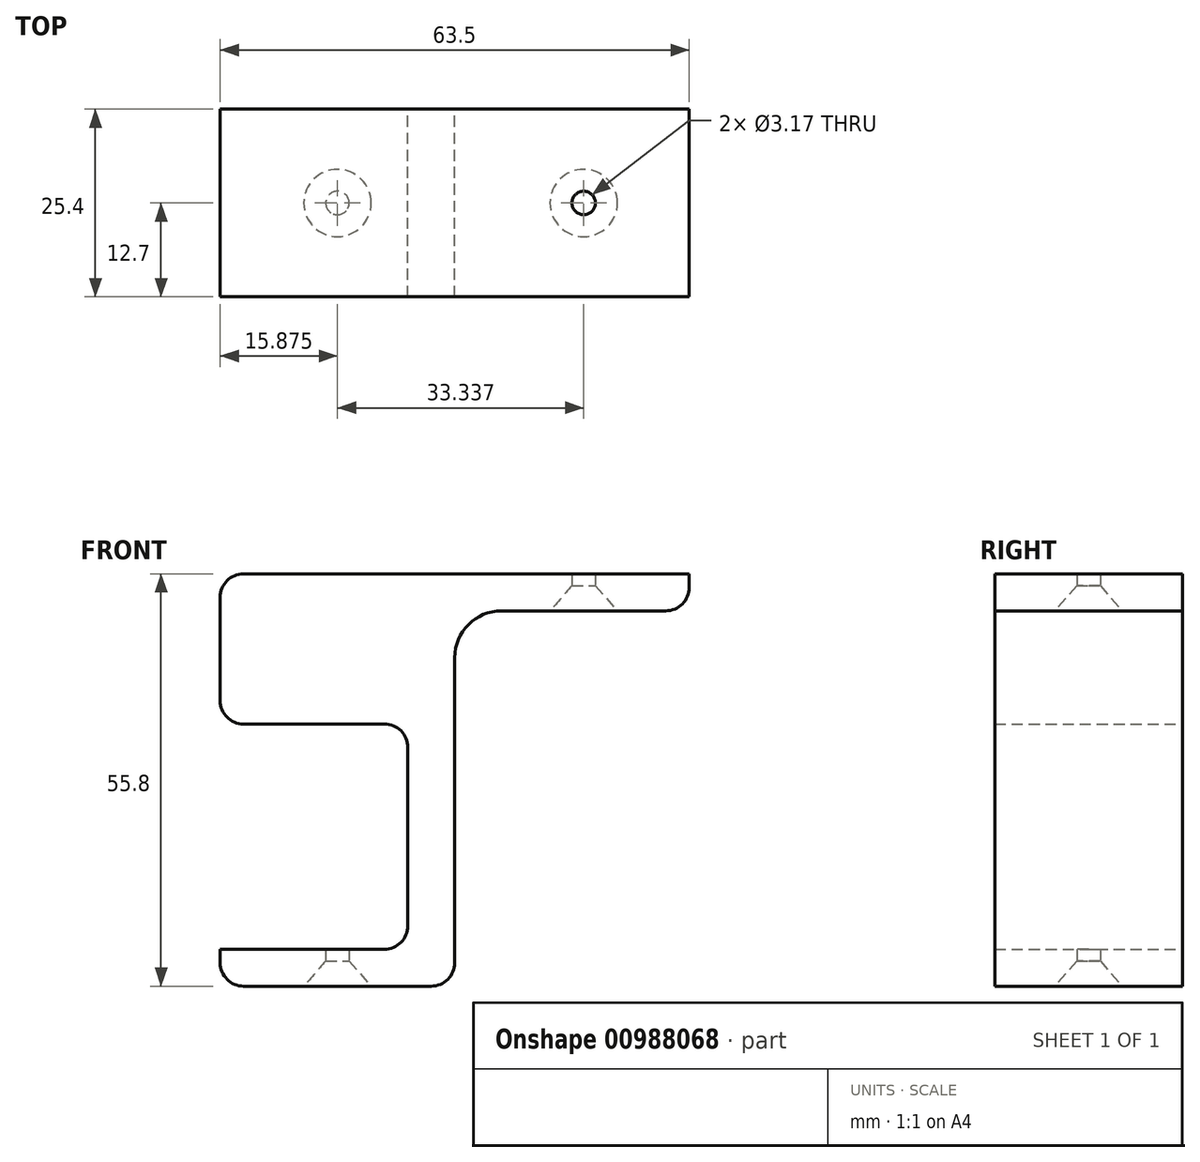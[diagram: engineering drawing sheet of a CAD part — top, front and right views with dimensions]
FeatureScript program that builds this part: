
annotation { "Feature Type Name" : "Feature", "Feature Type Description" : "" }
export const myFeature = defineFeature(function(context is Context, id is Id, definition is map)
    precondition{}
    {
        {
            var Q0;
            Q0=qCreatedBy(makeId("Front.planeOp"),FACE);
            var sketch = newSketch(context, id + "F0", { "sketchPlane" : qUnion([Q0])});
            skLineSegment(sketch, "E0", {"start": v(-25.4, -30.48) * mm, "end": v(-3.18, -30.48) * mm});
            skLineSegment(sketch, "E1", {"start": v(0, -27.3) * mm, "end": v(0, -3.17) * mm});
            skLineSegment(sketch, "E2", {"start": v(-3.18, 0) * mm, "end": v(-22.23, 0) * mm});
            skLineSegment(sketch, "E3", {"start": v(-25.4, 3.18) * mm, "end": v(-25.4, 17.15) * mm});
            skLineSegment(sketch, "E4", {"start": v(-22.22, 20.32) * mm, "end": v(38.1, 20.32) * mm});
            skLineSegment(sketch, "E5", {"start": v(38.1, 20.32) * mm, "end": v(38.1, 18.5) * mm});
            skLineSegment(sketch, "E6", {"start": v(34.92, 15.32) * mm, "end": v(12.7, 15.32) * mm});
            skLineSegment(sketch, "E7", {"start": v(6.35, 8.97) * mm, "end": v(6.35, -32.3) * mm});
            skLineSegment(sketch, "E8", {"start": v(3.18, -35.48) * mm, "end": v(-22.23, -35.48) * mm});
            skLineSegment(sketch, "E9", {"start": v(-25.4, -32.3) * mm, "end": v(-25.4, -30.48) * mm});
            skPoint(sketch, "E10.visualSharp", {"position": v(6.35, 15.32) * mm});
            skArc(sketch, "E10.filletArc", {"start": v(12.7, 15.32) * mm, "mid": v(8.2, 13.46) * mm, "end": v(6.35, 8.97) * mm});
            skPoint(sketch, "E11.visualSharp", {"position": v(0, 0) * mm});
            skArc(sketch, "E11.filletArc", {"start": v(0, -3.17) * mm, "mid": v(-0.93, -0.93) * mm, "end": v(-3.18, 0) * mm});
            skPoint(sketch, "E12.visualSharp", {"position": v(0, -30.48) * mm});
            skArc(sketch, "E12.filletArc", {"start": v(-3.18, -30.48) * mm, "mid": v(-0.93, -29.55) * mm, "end": v(0, -27.3) * mm});
            skPoint(sketch, "E13.visualSharp", {"position": v(-25.4, 20.32) * mm});
            skArc(sketch, "E13.filletArc", {"start": v(-22.22, 20.32) * mm, "mid": v(-24.47, 19.4) * mm, "end": v(-25.4, 17.15) * mm});
            skPoint(sketch, "E14.visualSharp", {"position": v(-25.4, 0) * mm});
            skArc(sketch, "E14.filletArc", {"start": v(-25.4, 3.17) * mm, "mid": v(-24.47, 0.93) * mm, "end": v(-22.23, 0) * mm});
            skPoint(sketch, "E15.visualSharp", {"position": v(-25.4, -35.48) * mm});
            skArc(sketch, "E15.filletArc", {"start": v(-25.4, -32.3) * mm, "mid": v(-24.47, -34.55) * mm, "end": v(-22.23, -35.48) * mm});
            skPoint(sketch, "E16.visualSharp", {"position": v(6.35, -35.48) * mm});
            skArc(sketch, "E16.filletArc", {"start": v(3.18, -35.48) * mm, "mid": v(5.42, -34.55) * mm, "end": v(6.35, -32.3) * mm});
            skPoint(sketch, "E17.visualSharp", {"position": v(38.1, 15.32) * mm});
            skArc(sketch, "E17.filletArc", {"start": v(34.92, 15.32) * mm, "mid": v(37.17, 16.25) * mm, "end": v(38.1, 18.5) * mm});
            skSolve(sketch);
        }
        {
            var Q0;
            Q0 = qSketchRegion(id + "F0", true);
            extrude(context, id + "F1", {"entities" : qUnion([Q0]), "endBound" : BoundingType.SYMMETRIC, "depth" : 25.4 * mm, "offsetDistance" : 25.4 * mm});
        }
        {
            var Q0;
            Q0=makeQuery(id+"F1.opExtrude","SWEPT_FACE",FACE,{"disambiguationData":[OSD([sQuery(id+"F0.wireOp",EDGE,"E8")])]});
            var sketch = newSketch(context, id + "F2", { "sketchPlane" : qUnion([Q0])});
            skPoint(sketch, "E18", {"position": v(-9.52, 0) * mm});
            skSolve(sketch);
        }
        {
            var Q0;
            Q0=makeQuery(id+"F1.opExtrude","SWEPT_FACE",FACE,{"disambiguationData":[OSD([sQuery(id+"F0.wireOp",EDGE,"E6")])]});
            var sketch = newSketch(context, id + "F3", { "sketchPlane" : qUnion([Q0])});
            skPoint(sketch, "E19", {"position": v(23.81, 0) * mm});
            skSolve(sketch);
        }
        {
            var Q0;
            Q0=sQuery(id+"F3.wireOp",VERTEX,"E19");
            var Q1;
            Q1=sQuery(id+"F2.wireOp",VERTEX,"E18");
            var Q2;
            Q2=makeQuery(id+"F1.opExtrude","SWEPT_BODY",BODY,{"disambiguationData":[OSD([sQuery(id+"F0.wireOp",EDGE,"E0"),sQuery(id+"F0.wireOp",EDGE,"E1"),sQuery(id+"F0.wireOp",EDGE,"E2"),sQuery(id+"F0.wireOp",EDGE,"E3"),sQuery(id+"F0.wireOp",EDGE,"E4"),sQuery(id+"F0.wireOp",EDGE,"E5"),sQuery(id+"F0.wireOp",EDGE,"E6"),sQuery(id+"F0.wireOp",EDGE,"E7"),sQuery(id+"F0.wireOp",EDGE,"E8"),sQuery(id+"F0.wireOp",EDGE,"E9"),sQuery(id+"F0.wireOp",EDGE,"E10.filletArc"),sQuery(id+"F0.wireOp",EDGE,"E11.filletArc"),sQuery(id+"F0.wireOp",EDGE,"E12.filletArc"),sQuery(id+"F0.wireOp",EDGE,"E13.filletArc"),sQuery(id+"F0.wireOp",EDGE,"E14.filletArc"),sQuery(id+"F0.wireOp",EDGE,"E15.filletArc"),sQuery(id+"F0.wireOp",EDGE,"E16.filletArc"),sQuery(id+"F0.wireOp",EDGE,"E17.filletArc")])]});
            hole(context, id + "F4", {"style" : HoleStyle.C_SINK, "endStyle" : HoleEndStyle.BLIND, "holeDiameter" : 3.17 * mm, "cSinkDiameter" : 9.12 * mm, "cSinkAngle" : 82 * degree, "majorDiameter" : 6.35 * mm, "holeDepth" : 25.4 * mm, "isTappedThrough" : true, "tappedDepth" : 3.5 * mm, "tapClearance" : 3, "locations" : qUnion([Q0, Q1]), "scope" : qUnion([Q2])});
        }
    });
